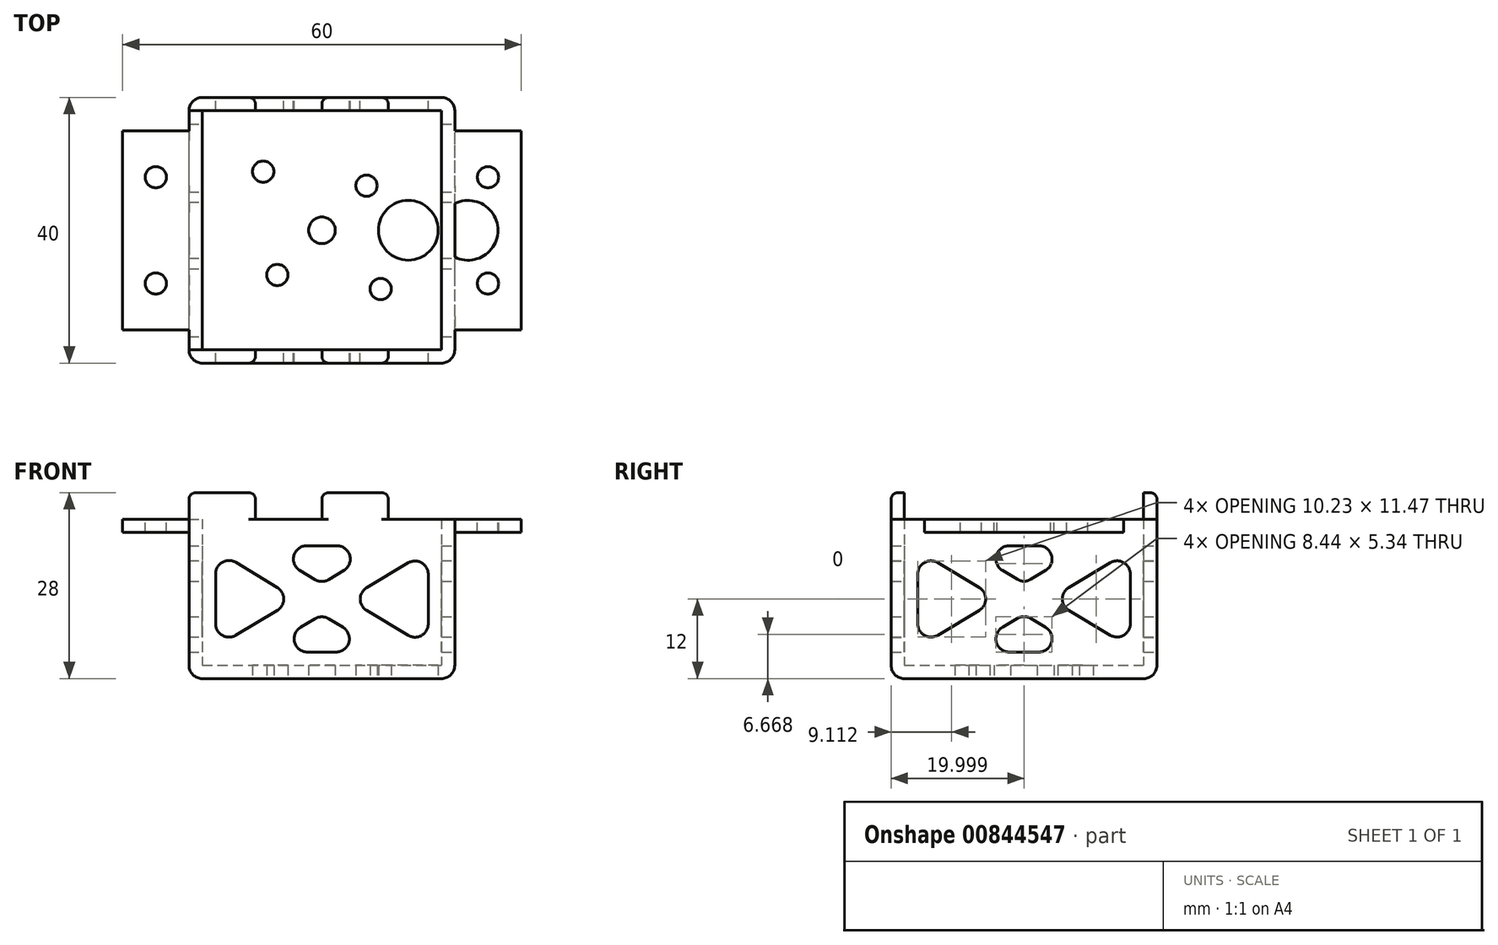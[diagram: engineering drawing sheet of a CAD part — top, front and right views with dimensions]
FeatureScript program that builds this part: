
annotation { "Feature Type Name" : "Feature", "Feature Type Description" : "" }
export const myFeature = defineFeature(function(context is Context, id is Id, definition is map)
    precondition{}
    {
        {
            var Q0;
            Q0=qCreatedBy(makeId("Top.planeOp"),FACE);
            var sketch = newSketch(context, id + "F0", { "sketchPlane" : qUnion([Q0])});
            skLineSegment(sketch, "E0.bottom", {"start": v(-66.54, 9.74) * mm, "end": v(-26.54, 9.74) * mm});
            skLineSegment(sketch, "E0.top", {"start": v(-66.54, 49.74) * mm, "end": v(-26.54, 49.74) * mm});
            skLineSegment(sketch, "E0.left", {"start": v(-66.54, 9.74) * mm, "end": v(-66.54, 49.74) * mm});
            skLineSegment(sketch, "E0.right", {"start": v(-26.54, 9.74) * mm, "end": v(-26.54, 49.74) * mm});
            skPoint(sketch, "E1", {"position": v(-46.54, 29.74) * mm});
            skPoint(sketch, "E1.positionSnap0", {"position": v(-46.54, 49.74) * mm});
            skPoint(sketch, "E1.positionSnap1", {"position": v(-26.54, 29.74) * mm});
            skPoint(sketch, "E2", {"position": v(-55.38, 38.58) * mm});
            skPoint(sketch, "E3", {"position": v(-37.7, 20.9) * mm});
            skPoint(sketch, "E4", {"position": v(-53.26, 23.02) * mm});
            skPoint(sketch, "E5", {"position": v(-39.82, 36.46) * mm});
            skPoint(sketch, "E6", {"position": v(-33.54, 29.74) * mm});
            skSolve(sketch);
        }
        {
            var Q0;
            Q0=makeQuery(id+"F0.imprint","IMPRINT",FACE,{"disambiguationData":[TD([[makeQuery(id+"F0.imprint","IMPRINT",EDGE,{"derivedFrom":sQuery(id+"F0.wireOp",EDGE,"E0.bottom")}),1.0]])]});
            extrude(context, id + "F1", {"entities" : qUnion([Q0]), "depth" : 2 * mm, "offsetDistance" : 25 * mm});
        }
        {
            var Q0;
            Q0=makeQuery(id+"F1.opExtrude","CAP_FACE",FACE,{"disambiguationData":[OSD([sQuery(id+"F0.wireOp",EDGE,"E0.bottom"),sQuery(id+"F0.wireOp",EDGE,"E0.top"),sQuery(id+"F0.wireOp",EDGE,"E0.left"),sQuery(id+"F0.wireOp",EDGE,"E0.right")])],"isStart":false});
            var sketch = newSketch(context, id + "F2", { "sketchPlane" : qUnion([Q0])});
            skLineSegment(sketch, "E7.bottom", {"start": v(-66.54, 9.74) * mm, "end": v(-26.54, 9.74) * mm});
            skLineSegment(sketch, "E7.top", {"start": v(-66.54, 49.74) * mm, "end": v(-26.54, 49.74) * mm});
            skLineSegment(sketch, "E7.left", {"start": v(-66.54, 9.74) * mm, "end": v(-66.54, 49.74) * mm});
            skLineSegment(sketch, "E7.right", {"start": v(-26.54, 9.74) * mm, "end": v(-26.54, 49.74) * mm});
            skLineSegment(sketch, "E8.0", {"start": v(-28.54, 11.74) * mm, "end": v(-28.54, 47.74) * mm});
            skLineSegment(sketch, "E8.1", {"start": v(-64.54, 11.74) * mm, "end": v(-28.54, 11.74) * mm});
            skLineSegment(sketch, "E8.2", {"start": v(-64.54, 11.74) * mm, "end": v(-64.54, 47.74) * mm});
            skLineSegment(sketch, "E8.3", {"start": v(-64.54, 47.74) * mm, "end": v(-28.54, 47.74) * mm});
            skSolve(sketch);
        }
        {
            var Q0;
            Q0=makeQuery(id+"F2.imprint","IMPRINT",FACE,{"disambiguationData":[TD([[makeQuery(id+"F2.imprint","IMPRINT",EDGE,{"derivedFrom":sQuery(id+"F2.wireOp",EDGE,"E7.bottom")}),1.0]])]});
            extrude(context, id + "F3", {"entities" : qUnion([Q0]), "operationType" : NewBodyOperationType.ADD, "depth" : 22 * mm, "offsetDistance" : 25 * mm});
        }
        {
            var Q0;
            Q0=makeQuery(id+"F3.boolean.opBoolean","MERGE",FACE,{"derivedFrom":[makeQuery(id+"F1.opExtrude","SWEPT_FACE",FACE,{"disambiguationData":[OSD([sQuery(id+"F0.wireOp",EDGE,"E0.bottom")])]}),makeQuery(id+"F3.opExtrude","SWEPT_FACE",FACE,{"disambiguationData":[OSD([sQuery(id+"F2.wireOp",EDGE,"E7.bottom")])]})]});
            var sketch = newSketch(context, id + "F4", { "sketchPlane" : qUnion([Q0])});
            skLineSegment(sketch, "E9", {"start": v(-66.54, 24) * mm, "end": v(-66.54, 28) * mm});
            skLineSegment(sketch, "E10", {"start": v(-66.54, 28) * mm, "end": v(-56.54, 28) * mm});
            skLineSegment(sketch, "E11", {"start": v(-56.54, 28) * mm, "end": v(-56.54, 24) * mm});
            skLineSegment(sketch, "E12.MirrorCS", {"start": v(-36.54, 28) * mm, "end": v(-46.54, 28) * mm});
            skLineSegment(sketch, "E13.MirrorCS", {"start": v(-46.54, 28) * mm, "end": v(-46.54, 24) * mm});
            skLineSegment(sketch, "E14.MirrorCS", {"start": v(-36.54, 24) * mm, "end": v(-36.54, 28) * mm});
            skSolve(sketch);
        }
        {
            var Q0;
            Q0=makeQuery(id+"F4.imprint","IMPRINT",FACE,{"disambiguationData":[TD([[makeQuery(id+"F4.imprint","IMPRINT",EDGE,{"derivedFrom":sQuery(id+"F4.wireOp",EDGE,"E12.MirrorCS")}),1.0]])]});
            var Q1;
            {var subQ0=sQuery(id+"F4.wireOp",EDGE,"E9");Q1=makeQuery(id+"F4.imprint","IMPRINT",FACE,{"disambiguationData":[TD([[makeQuery(id+"F4.imprint","IMPRINT",EDGE,{"derivedFrom":subQ0}),-1.0]])]});}
            var Q2;
            Q2=makeQuery(id+"F3.opExtrude","SWEPT_FACE",FACE,{"disambiguationData":[OSD([sQuery(id+"F2.wireOp",EDGE,"E8.1")])]});
            extrude(context, id + "F5", {"entities" : qUnion([Q0, Q1]), "operationType" : NewBodyOperationType.ADD, "endBound" : BoundingType.UP_TO_SURFACE, "oppositeDirection" : true, "depth" : 8.5 * mm, "endBoundEntityFace" : qUnion([Q2]), "offsetDistance" : 25 * mm});
        }
        {
            var Q0;
            Q0=makeQuery(id+"F3.boolean.opBoolean","MERGE",FACE,{"derivedFrom":[makeQuery(id+"F1.opExtrude","SWEPT_FACE",FACE,{"disambiguationData":[OSD([sQuery(id+"F0.wireOp",EDGE,"E0.top")])]}),makeQuery(id+"F3.opExtrude","SWEPT_FACE",FACE,{"disambiguationData":[OSD([sQuery(id+"F2.wireOp",EDGE,"E7.top")])]})]});
            var sketch = newSketch(context, id + "F6", { "sketchPlane" : qUnion([Q0])});
            skLineSegment(sketch, "E15", {"start": v(36.54, 24) * mm, "end": v(36.54, 28) * mm});
            skLineSegment(sketch, "E16", {"start": v(36.54, 28) * mm, "end": v(46.54, 28) * mm});
            skLineSegment(sketch, "E17", {"start": v(46.54, 28) * mm, "end": v(46.54, 24) * mm});
            skLineSegment(sketch, "E18", {"start": v(56.54, 24) * mm, "end": v(56.54, 28) * mm});
            skLineSegment(sketch, "E19", {"start": v(56.54, 28) * mm, "end": v(66.54, 28) * mm});
            skLineSegment(sketch, "E20", {"start": v(66.54, 28) * mm, "end": v(66.54, 24) * mm});
            skSolve(sketch);
        }
        {
            var Q0;
            {var subQ0=sQuery(id+"F6.wireOp",EDGE,"E15");Q0=makeQuery(id+"F6.imprint","IMPRINT",FACE,{"disambiguationData":[TD([[makeQuery(id+"F6.imprint","IMPRINT",EDGE,{"derivedFrom":subQ0}),-1.0]])]});}
            var Q1;
            {var subQ0=sQuery(id+"F6.wireOp",EDGE,"E18");Q1=makeQuery(id+"F6.imprint","IMPRINT",FACE,{"disambiguationData":[TD([[makeQuery(id+"F6.imprint","IMPRINT",EDGE,{"derivedFrom":subQ0}),-1.0]])]});}
            var Q2;
            Q2=makeQuery(id+"F3.opExtrude","SWEPT_FACE",FACE,{"disambiguationData":[OSD([sQuery(id+"F2.wireOp",EDGE,"E8.3")])]});
            extrude(context, id + "F7", {"entities" : qUnion([Q0, Q1]), "operationType" : NewBodyOperationType.ADD, "endBound" : BoundingType.UP_TO_SURFACE, "oppositeDirection" : true, "depth" : 25 * mm, "endBoundEntityFace" : qUnion([Q2]), "offsetDistance" : 25 * mm});
        }
        {
            var Q0;
            {var subQ0=sQuery(id+"F2.wireOp",EDGE,"E8.3");var subQ2=sQuery(id+"F2.wireOp",EDGE,"E8.1");var subQ5=sQuery(id+"F2.wireOp",EDGE,"E7.bottom");var subQ7=sQuery(id+"F2.wireOp",EDGE,"E8.0");var subQ9=sQuery(id+"F2.wireOp",EDGE,"E7.right");var subQ11=sQuery(id+"F2.wireOp",EDGE,"E7.top");var subQ15=makeQuery(id+"F1.opExtrude","SWEPT_FACE",FACE,{"disambiguationData":[OSD([sQuery(id+"F0.wireOp",EDGE,"E0.right")])]});var subQ17=makeQuery(id+"F1.opExtrude","SWEPT_FACE",FACE,{"disambiguationData":[OSD([sQuery(id+"F0.wireOp",EDGE,"E0.top")])]});var subQ23=sQuery(id+"F2.wireOp",EDGE,"E7.left");var subQ24=sQuery(id+"F2.wireOp",EDGE,"E8.2");Q0=makeQuery(id+"F7.boolean.opBoolean","SPLIT",FACE,{"disambiguationData":[TD([subQ15])],"derivedFrom":makeQuery(id+"F5.boolean.opBoolean","SPLIT",FACE,{"disambiguationData":[TD([subQ17])],"derivedFrom":makeQuery(id+"F3.opExtrude","CAP_FACE",FACE,{"disambiguationData":[OSD([subQ5,subQ11,subQ23,subQ9,subQ7,subQ2,subQ24,subQ0])],"isStart":false})})});}
            var sketch = newSketch(context, id + "F8", { "sketchPlane" : qUnion([Q0])});
            skLineSegment(sketch, "E21", {"start": v(-26.54, 44.74) * mm, "end": v(-16.54, 44.74) * mm});
            skLineSegment(sketch, "E22", {"start": v(-16.54, 44.74) * mm, "end": v(-16.54, 14.74) * mm});
            skLineSegment(sketch, "E23", {"start": v(-16.54, 14.74) * mm, "end": v(-26.54, 14.74) * mm});
            skPoint(sketch, "E24", {"position": v(-21.54, 21.74) * mm});
            skPoint(sketch, "E24.positionSnap0", {"position": v(-21.54, 14.74) * mm});
            skPoint(sketch, "E25", {"position": v(-21.54, 37.74) * mm});
            skPoint(sketch, "E26", {"position": v(-24.54, 29.74) * mm});
            skPoint(sketch, "E26.positionSnap0", {"position": v(-26.54, 29.74) * mm});
            skCircle(sketch, "E27", {"center": v(-24.54, 29.74) * mm, "radius": 4.5 * mm});
            skSolve(sketch);
        }
        {
            var Q0;
            {var subQ0=sQuery(id+"F8.wireOp",EDGE,"E21");Q0=makeQuery(id+"F8.imprint","IMPRINT",FACE,{"disambiguationData":[TD([[makeQuery(id+"F8.imprint","IMPRINT",EDGE,{"derivedFrom":subQ0}),-1.0]])]});}
            extrude(context, id + "F9", {"entities" : qUnion([Q0]), "operationType" : NewBodyOperationType.ADD, "oppositeDirection" : true, "depth" : 2 * mm, "offsetDistance" : 25 * mm});
        }
        {
            var Q0;
            {var subQ2=sQuery(id+"F2.wireOp",EDGE,"E8.3");var subQ4=sQuery(id+"F2.wireOp",EDGE,"E8.2");var subQ7=sQuery(id+"F2.wireOp",EDGE,"E7.top");var subQ8=sQuery(id+"F2.wireOp",EDGE,"E8.1");var subQ10=sQuery(id+"F2.wireOp",EDGE,"E7.left");var subQ13=makeQuery(id+"F1.opExtrude","SWEPT_FACE",FACE,{"disambiguationData":[OSD([sQuery(id+"F0.wireOp",EDGE,"E0.top")])]});var subQ14=sQuery(id+"F2.wireOp",EDGE,"E7.bottom");var subQ16=makeQuery(id+"F1.opExtrude","SWEPT_FACE",FACE,{"disambiguationData":[OSD([sQuery(id+"F0.wireOp",EDGE,"E0.left")])]});var subQ23=sQuery(id+"F2.wireOp",EDGE,"E8.0");var subQ24=sQuery(id+"F2.wireOp",EDGE,"E7.right");Q0=makeQuery(id+"F7.boolean.opBoolean","SPLIT",FACE,{"disambiguationData":[TD([subQ16])],"derivedFrom":makeQuery(id+"F5.boolean.opBoolean","SPLIT",FACE,{"disambiguationData":[TD([subQ13])],"derivedFrom":makeQuery(id+"F3.opExtrude","CAP_FACE",FACE,{"disambiguationData":[OSD([subQ14,subQ7,subQ10,subQ24,subQ23,subQ8,subQ4,subQ2])],"isStart":false})})});}
            var sketch = newSketch(context, id + "F10", { "sketchPlane" : qUnion([Q0])});
            skLineSegment(sketch, "E28", {"start": v(-76.54, 44.74) * mm, "end": v(-76.54, 14.74) * mm});
            skLineSegment(sketch, "E29", {"start": v(-76.54, 14.74) * mm, "end": v(-66.54, 14.74) * mm});
            skLineSegment(sketch, "E30", {"start": v(-66.54, 44.74) * mm, "end": v(-76.54, 44.74) * mm});
            skPoint(sketch, "E31", {"position": v(-71.54, 21.74) * mm});
            skPoint(sketch, "E31.positionSnap0", {"position": v(-71.54, 14.74) * mm});
            skPoint(sketch, "E32", {"position": v(-71.54, 37.74) * mm});
            skSolve(sketch);
        }
        {
            var Q0;
            Q0=makeQuery(id+"F10.imprint","IMPRINT",FACE,{"disambiguationData":[TD([[makeQuery(id+"F10.imprint","IMPRINT",EDGE,{"derivedFrom":sQuery(id+"F10.wireOp",EDGE,"E28")}),1.0]])]});
            extrude(context, id + "F11", {"entities" : qUnion([Q0]), "operationType" : NewBodyOperationType.ADD, "oppositeDirection" : true, "depth" : 2 * mm, "offsetDistance" : 25 * mm});
        }
        {
            var Q0;
            Q0=sQuery(id+"F8.wireOp",VERTEX,"E24");
            var Q1;
            Q1=sQuery(id+"F8.wireOp",VERTEX,"E25");
            var Q2;
            Q2=sQuery(id+"F10.wireOp",VERTEX,"E31");
            var Q3;
            Q3=sQuery(id+"F10.wireOp",VERTEX,"E32");
            var Q4;
            Q4=makeQuery(id+"F1.opExtrude","SWEPT_BODY",BODY,{"disambiguationData":[OSD([sQuery(id+"F0.wireOp",EDGE,"E0.bottom"),sQuery(id+"F0.wireOp",EDGE,"E0.top"),sQuery(id+"F0.wireOp",EDGE,"E0.left"),sQuery(id+"F0.wireOp",EDGE,"E0.right")])]});
            hole(context, id + "F12", {"style" : HoleStyle.SIMPLE, "endStyle" : HoleEndStyle.THROUGH, "holeDiameter" : 3.2 * mm, "majorDiameter" : 5 * mm, "isTappedThrough" : true, "tappedDepth" : 12 * mm, "tapClearance" : 3, "startFromSketch" : true, "locations" : qUnion([Q0, Q1, Q2, Q3]), "scope" : qUnion([Q4])});
        }
        {
            var Q0;
            Q0=sQuery(id+"F0.wireOp",VERTEX,"E5");
            var Q1;
            Q1=sQuery(id+"F0.wireOp",VERTEX,"E2");
            var Q2;
            Q2=sQuery(id+"F0.wireOp",VERTEX,"E4");
            var Q3;
            Q3=sQuery(id+"F0.wireOp",VERTEX,"E3");
            var Q4;
            Q4=makeQuery(id+"F1.opExtrude","SWEPT_BODY",BODY,{"disambiguationData":[OSD([sQuery(id+"F0.wireOp",EDGE,"E0.bottom"),sQuery(id+"F0.wireOp",EDGE,"E0.top"),sQuery(id+"F0.wireOp",EDGE,"E0.left"),sQuery(id+"F0.wireOp",EDGE,"E0.right")])]});
            hole(context, id + "F13", {"style" : HoleStyle.SIMPLE, "endStyle" : HoleEndStyle.THROUGH, "oppositeDirection" : true, "holeDiameter" : 3.2 * mm, "majorDiameter" : 5 * mm, "isTappedThrough" : true, "tappedDepth" : 12 * mm, "tapClearance" : 3, "startFromSketch" : true, "locations" : qUnion([Q0, Q1, Q2, Q3]), "scope" : qUnion([Q4])});
        }
        {
            var Q0;
            Q0=sQuery(id+"F0.wireOp",VERTEX,"E6");
            var Q1;
            Q1=makeQuery(id+"F1.opExtrude","SWEPT_BODY",BODY,{"disambiguationData":[OSD([sQuery(id+"F0.wireOp",EDGE,"E0.bottom"),sQuery(id+"F0.wireOp",EDGE,"E0.top"),sQuery(id+"F0.wireOp",EDGE,"E0.left"),sQuery(id+"F0.wireOp",EDGE,"E0.right")])]});
            hole(context, id + "F14", {"style" : HoleStyle.SIMPLE, "endStyle" : HoleEndStyle.THROUGH, "oppositeDirection" : true, "holeDiameter" : 9 * mm, "majorDiameter" : 5 * mm, "isTappedThrough" : true, "tappedDepth" : 12 * mm, "tapClearance" : 3, "startFromSketch" : true, "locations" : qUnion([Q0]), "scope" : qUnion([Q1])});
        }
        {
            var Q0;
            Q0=sQuery(id+"F0.wireOp",VERTEX,"E1");
            var Q1;
            Q1=makeQuery(id+"F1.opExtrude","SWEPT_BODY",BODY,{"disambiguationData":[OSD([sQuery(id+"F0.wireOp",EDGE,"E0.bottom"),sQuery(id+"F0.wireOp",EDGE,"E0.top"),sQuery(id+"F0.wireOp",EDGE,"E0.left"),sQuery(id+"F0.wireOp",EDGE,"E0.right")])]});
            hole(context, id + "F15", {"style" : HoleStyle.SIMPLE, "endStyle" : HoleEndStyle.THROUGH, "oppositeDirection" : true, "holeDiameter" : 4 * mm, "majorDiameter" : 5 * mm, "isTappedThrough" : true, "tappedDepth" : 12 * mm, "tapClearance" : 3, "startFromSketch" : true, "locations" : qUnion([Q0]), "scope" : qUnion([Q1])});
        }
        {
            var Q0;
            Q0=makeQuery(id+"F7.opExtrude","CAP_EDGE",EDGE,{"disambiguationData":[OSD([sQuery(id+"F6.wireOp",EDGE,"E15")])],"isStart":true});
            var Q1;
            Q1=makeQuery(id+"F7.opExtrude","TWEAK_EDGE",EDGE,{"derivedFrom":[makeQuery(id+"F3.opExtrude","SWEPT_FACE",FACE,{"disambiguationData":[OSD([sQuery(id+"F2.wireOp",EDGE,"E8.3")])]}),makeQuery(id+"F6.imprint","IMPRINT",EDGE,{"derivedFrom":sQuery(id+"F6.wireOp",EDGE,"E15")})]});
            var Q2;
            Q2=makeQuery(id+"F7.opExtrude","CAP_EDGE",EDGE,{"disambiguationData":[OSD([sQuery(id+"F6.wireOp",EDGE,"E17")])],"isStart":true});
            var Q3;
            Q3=makeQuery(id+"F7.opExtrude","TWEAK_EDGE",EDGE,{"derivedFrom":[makeQuery(id+"F3.opExtrude","SWEPT_FACE",FACE,{"disambiguationData":[OSD([sQuery(id+"F2.wireOp",EDGE,"E8.3")])]}),makeQuery(id+"F6.imprint","IMPRINT",EDGE,{"derivedFrom":sQuery(id+"F6.wireOp",EDGE,"E17")})]});
            var Q4;
            Q4=makeQuery(id+"F7.opExtrude","TWEAK_EDGE",EDGE,{"derivedFrom":[makeQuery(id+"F3.opExtrude","SWEPT_FACE",FACE,{"disambiguationData":[OSD([sQuery(id+"F2.wireOp",EDGE,"E8.3")])]}),makeQuery(id+"F6.imprint","IMPRINT",EDGE,{"derivedFrom":sQuery(id+"F6.wireOp",EDGE,"E18")})]});
            var Q5;
            Q5=makeQuery(id+"F7.opExtrude","CAP_EDGE",EDGE,{"disambiguationData":[OSD([sQuery(id+"F6.wireOp",EDGE,"E18")])],"isStart":true});
            var Q6;
            Q6=makeQuery(id+"F5.opExtrude","CAP_EDGE",EDGE,{"disambiguationData":[OSD([sQuery(id+"F4.wireOp",EDGE,"E11")])],"isStart":true});
            var Q7;
            Q7=makeQuery(id+"F5.opExtrude","CAP_EDGE",EDGE,{"disambiguationData":[OSD([sQuery(id+"F4.wireOp",EDGE,"E13.MirrorCS")])],"isStart":true});
            var Q8;
            Q8=makeQuery(id+"F5.opExtrude","CAP_EDGE",EDGE,{"disambiguationData":[OSD([sQuery(id+"F4.wireOp",EDGE,"E14.MirrorCS")])],"isStart":true});
            var Q9;
            {var subQ0=sQuery(id+"F4.wireOp",EDGE,"E14.MirrorCS");Q9=makeQuery(id+"F5.opExtrude","TWEAK_EDGE",EDGE,{"derivedFrom":[makeQuery(id+"F3.opExtrude","SWEPT_FACE",FACE,{"disambiguationData":[OSD([sQuery(id+"F2.wireOp",EDGE,"E8.1")])]}),makeQuery(id+"F4.imprint","IMPRINT",EDGE,{"disambiguationData":[TD([[makeQuery(id+"F4.imprint","INTERSECT",VERTEX,{"derivedFrom":[sQuery(id+"F4.wireOp",EDGE,"E12.MirrorCS"),subQ0]}),1.0]])],"derivedFrom":subQ0})]});}
            var Q10;
            Q10=makeQuery(id+"F5.opExtrude","TWEAK_EDGE",EDGE,{"derivedFrom":[makeQuery(id+"F3.opExtrude","SWEPT_FACE",FACE,{"disambiguationData":[OSD([sQuery(id+"F2.wireOp",EDGE,"E8.1")])]}),makeQuery(id+"F4.imprint","IMPRINT",EDGE,{"derivedFrom":sQuery(id+"F4.wireOp",EDGE,"E11")})]});
            var Q11;
            Q11=makeQuery(id+"F5.opExtrude","TWEAK_EDGE",EDGE,{"derivedFrom":[makeQuery(id+"F3.opExtrude","SWEPT_FACE",FACE,{"disambiguationData":[OSD([sQuery(id+"F2.wireOp",EDGE,"E8.1")])]}),makeQuery(id+"F4.imprint","IMPRINT",EDGE,{"derivedFrom":sQuery(id+"F4.wireOp",EDGE,"E13.MirrorCS")})]});
            fillet(context, id + "F16", {"entities" : qUnion([Q0, Q1, Q2, Q3, Q4, Q5, Q6, Q7, Q8, Q9, Q10, Q11]), "radius" : 1 * mm, "tangentPropagation" : true, "allowEdgeOverflow" : false});
        }
        {
            var Q0;
            Q0=makeQuery(id+"F3.boolean.opBoolean","MERGE",FACE,{"derivedFrom":[makeQuery(id+"F1.opExtrude","SWEPT_FACE",FACE,{"disambiguationData":[OSD([sQuery(id+"F0.wireOp",EDGE,"E0.right")])]}),makeQuery(id+"F3.opExtrude","SWEPT_FACE",FACE,{"disambiguationData":[OSD([sQuery(id+"F2.wireOp",EDGE,"E7.right")])]})]});
            var sketch = newSketch(context, id + "F17", { "sketchPlane" : qUnion([Q0])});
            skLineSegment(sketch, "E33.0", {"start": v(13.74, 24) * mm, "end": v(13.74, 23.93) * mm});
            skLineSegment(sketch, "E34.0", {"start": v(27.51, 20) * mm, "end": v(31.96, 20) * mm});
            skLineSegment(sketch, "E35.0", {"start": v(42.71, 17.45) * mm, "end": v(36.48, 13.71) * mm});
            skLineSegment(sketch, "E36.0", {"start": v(33, 16.29) * mm, "end": v(30.77, 14.95) * mm});
            skLineSegment(sketch, "E37.trimOffspring", {"start": v(29.74, 12) * mm, "end": v(29.74, 12) * mm});
            skLineSegment(sketch, "E38.trimOffspring", {"start": v(36.48, 10.29) * mm, "end": v(42.71, 6.55) * mm});
            skLineSegment(sketch, "E39.trimOffspring", {"start": v(31.68, 13.17) * mm, "end": v(31.69, 13.16) * mm});
            skLineSegment(sketch, "E40.trimOffspring", {"start": v(23, 10.29) * mm, "end": v(16.77, 6.55) * mm});
            skLineSegment(sketch, "E41.trimOffspring", {"start": v(30.77, 9.05) * mm, "end": v(33, 7.71) * mm});
            skLineSegment(sketch, "E42.trimOffspring", {"start": v(28.71, 9.05) * mm, "end": v(26.48, 7.71) * mm});
            skLineSegment(sketch, "E43.trimOffspring", {"start": v(45.74, 15.74) * mm, "end": v(45.74, 8.26) * mm});
            skLineSegment(sketch, "E44.trimOffspring", {"start": v(26.48, 16.29) * mm, "end": v(28.71, 14.95) * mm});
            skLineSegment(sketch, "E45.trimOffspring", {"start": v(45.74, 0.07) * mm, "end": v(45.74, 0) * mm});
            skLineSegment(sketch, "E46.trimOffspring", {"start": v(27.51, 4) * mm, "end": v(31.96, 4) * mm});
            skLineSegment(sketch, "E47.trimOffspring", {"start": v(16.4, 4) * mm, "end": v(16.41, 4) * mm});
            skLineSegment(sketch, "E48.trimOffspring", {"start": v(13.74, 15.74) * mm, "end": v(13.74, 8.26) * mm});
            skLineSegment(sketch, "E49", {"start": v(16.77, 17.45) * mm, "end": v(23, 13.71) * mm});
            skPoint(sketch, "E50.visualSharp", {"position": v(25.85, 12) * mm});
            skArc(sketch, "E50.filletArc", {"start": v(23, 10.29) * mm, "mid": v(23.96, 12) * mm, "end": v(23, 13.71) * mm});
            skPoint(sketch, "E51.visualSharp", {"position": v(13.74, 19.27) * mm});
            skArc(sketch, "E51.filletArc", {"start": v(16.77, 17.45) * mm, "mid": v(14.75, 17.48) * mm, "end": v(13.74, 15.74) * mm});
            skPoint(sketch, "E52.visualSharp", {"position": v(13.74, 4.73) * mm});
            skArc(sketch, "E52.filletArc", {"start": v(13.74, 8.26) * mm, "mid": v(14.75, 6.52) * mm, "end": v(16.77, 6.55) * mm});
            skPoint(sketch, "E53.visualSharp", {"position": v(29.74, 14.33) * mm});
            skArc(sketch, "E53.filletArc", {"start": v(28.71, 14.95) * mm, "mid": v(29.74, 14.66) * mm, "end": v(30.77, 14.95) * mm});
            skPoint(sketch, "E54.visualSharp", {"position": v(39.19, 20) * mm});
            skArc(sketch, "E54.filletArc", {"start": v(33, 16.29) * mm, "mid": v(33.9, 18.53) * mm, "end": v(31.96, 20) * mm});
            skPoint(sketch, "E55.visualSharp", {"position": v(20.3, 20) * mm});
            skArc(sketch, "E55.filletArc", {"start": v(27.51, 20) * mm, "mid": v(25.59, 18.53) * mm, "end": v(26.48, 16.29) * mm});
            skPoint(sketch, "E56.visualSharp", {"position": v(33.63, 12) * mm});
            skArc(sketch, "E56.filletArc", {"start": v(36.48, 13.71) * mm, "mid": v(35.51, 12) * mm, "end": v(36.48, 10.29) * mm});
            skPoint(sketch, "E57.visualSharp", {"position": v(45.74, 4.73) * mm});
            skArc(sketch, "E57.filletArc", {"start": v(42.71, 6.55) * mm, "mid": v(44.72, 6.52) * mm, "end": v(45.74, 8.26) * mm});
            skPoint(sketch, "E58.visualSharp", {"position": v(45.74, 19.27) * mm});
            skArc(sketch, "E58.filletArc", {"start": v(45.74, 15.74) * mm, "mid": v(44.72, 17.48) * mm, "end": v(42.71, 17.45) * mm});
            skPoint(sketch, "E59.visualSharp", {"position": v(29.74, 9.67) * mm});
            skArc(sketch, "E59.filletArc", {"start": v(30.77, 9.05) * mm, "mid": v(29.74, 9.34) * mm, "end": v(28.71, 9.05) * mm});
            skPoint(sketch, "E60.visualSharp", {"position": v(20.3, 4) * mm});
            skArc(sketch, "E60.filletArc", {"start": v(26.48, 7.71) * mm, "mid": v(25.59, 5.47) * mm, "end": v(27.51, 4) * mm});
            skPoint(sketch, "E61.visualSharp", {"position": v(39.19, 4) * mm});
            skArc(sketch, "E61.filletArc", {"start": v(31.96, 4) * mm, "mid": v(33.9, 5.47) * mm, "end": v(33, 7.71) * mm});
            skSolve(sketch);
        }
        {
            var Q0;
            Q0=makeQuery(id+"F17.imprint","IMPRINT",FACE,{"disambiguationData":[TD([[makeQuery(id+"F17.imprint","IMPRINT",EDGE,{"derivedFrom":sQuery(id+"F17.wireOp",EDGE,"E40.trimOffspring")}),-1.0]])]});
            var Q1;
            Q1=makeQuery(id+"F17.imprint","IMPRINT",FACE,{"disambiguationData":[TD([[makeQuery(id+"F17.imprint","IMPRINT",EDGE,{"derivedFrom":sQuery(id+"F17.wireOp",EDGE,"E34.0")}),-1.0]])]});
            var Q2;
            Q2=makeQuery(id+"F17.imprint","IMPRINT",FACE,{"disambiguationData":[TD([[makeQuery(id+"F17.imprint","IMPRINT",EDGE,{"derivedFrom":sQuery(id+"F17.wireOp",EDGE,"E35.0")}),1.0]])]});
            var Q3;
            Q3=makeQuery(id+"F17.imprint","IMPRINT",FACE,{"disambiguationData":[TD([[makeQuery(id+"F17.imprint","IMPRINT",EDGE,{"derivedFrom":sQuery(id+"F17.wireOp",EDGE,"E41.trimOffspring")}),-1.0]])]});
            var Q4;
            Q4=makeQuery(id+"F7.boolean.opBoolean","MERGE",FACE,{"derivedFrom":[makeQuery(id+"F5.boolean.opBoolean","MERGE",FACE,{"derivedFrom":[makeQuery(id+"F3.boolean.opBoolean","MERGE",FACE,{"derivedFrom":[makeQuery(id+"F1.opExtrude","SWEPT_FACE",FACE,{"disambiguationData":[OSD([sQuery(id+"F0.wireOp",EDGE,"E0.left")])]}),makeQuery(id+"F3.opExtrude","SWEPT_FACE",FACE,{"disambiguationData":[OSD([sQuery(id+"F2.wireOp",EDGE,"E7.left")])]})]}),makeQuery(id+"F5.opExtrude","SWEPT_FACE",FACE,{"disambiguationData":[OSD([sQuery(id+"F4.wireOp",EDGE,"E9")])]})]}),makeQuery(id+"F7.opExtrude","SWEPT_FACE",FACE,{"disambiguationData":[OSD([sQuery(id+"F6.wireOp",EDGE,"E20")])]})]});
            extrude(context, id + "F18", {"entities" : qUnion([Q0, Q1, Q2, Q3]), "operationType" : NewBodyOperationType.REMOVE, "endBound" : BoundingType.UP_TO_SURFACE, "oppositeDirection" : true, "depth" : 25 * mm, "endBoundEntityFace" : qUnion([Q4]), "offsetDistance" : 25 * mm});
        }
        {
            var Q0;
            {var subQ0=sQuery(id+"F2.wireOp",EDGE,"E7.top");Q0=makeQuery(id+"F7.boolean.opBoolean","MERGE",FACE,{"derivedFrom":[makeQuery(id+"F3.boolean.opBoolean","MERGE",FACE,{"derivedFrom":[makeQuery(id+"F1.opExtrude","SWEPT_FACE",FACE,{"disambiguationData":[OSD([sQuery(id+"F0.wireOp",EDGE,"E0.top")])]}),makeQuery(id+"F3.opExtrude","SWEPT_FACE",FACE,{"disambiguationData":[OSD([subQ0])]})]}),makeQuery(id+"F7.opExtrude","CAP_FACE",FACE,{"disambiguationData":[OSD([subQ0,sQuery(id+"F6.wireOp",EDGE,"E15"),sQuery(id+"F6.wireOp",EDGE,"E16"),sQuery(id+"F6.wireOp",EDGE,"E17")])],"isStart":true}),makeQuery(id+"F7.opExtrude","CAP_FACE",FACE,{"disambiguationData":[OSD([subQ0,sQuery(id+"F6.wireOp",EDGE,"E18"),sQuery(id+"F6.wireOp",EDGE,"E19"),sQuery(id+"F6.wireOp",EDGE,"E20")])],"isStart":true})]});}
            var sketch = newSketch(context, id + "F19", { "sketchPlane" : qUnion([Q0])});
            skLineSegment(sketch, "E62.0", {"start": v(43.37, 7.71) * mm, "end": v(45.52, 9.01) * mm});
            skLineSegment(sketch, "E63.0", {"start": v(33.57, 6.51) * mm, "end": v(39.8, 10.26) * mm});
            skLineSegment(sketch, "E64.0", {"start": v(33.57, 17.43) * mm, "end": v(39.8, 13.69) * mm});
            skPoint(sketch, "E65.orphan", {"position": v(66.54, 24) * mm});
            skLineSegment(sketch, "E66.trimOffspring", {"start": v(53.25, 13.7) * mm, "end": v(59.5, 17.5) * mm});
            skLineSegment(sketch, "E67.trimOffspring", {"start": v(53.26, 10.28) * mm, "end": v(59.51, 6.53) * mm});
            skLineSegment(sketch, "E68.trimOffspring", {"start": v(47.58, 9.02) * mm, "end": v(49.75, 7.71) * mm});
            skLineSegment(sketch, "E69.trimOffspring", {"start": v(47.58, 14.92) * mm, "end": v(49.85, 16.29) * mm});
            skLineSegment(sketch, "E70.0", {"start": v(62.54, 15.78) * mm, "end": v(62.54, 8.24) * mm});
            skLineSegment(sketch, "E71.0", {"start": v(30.54, 24) * mm, "end": v(30.54, 23.9) * mm});
            skLineSegment(sketch, "E72.0", {"start": v(48.83, 20) * mm, "end": v(44.27, 20) * mm});
            skLineSegment(sketch, "E73.trimOffspring", {"start": v(62.54, 0.04) * mm, "end": v(62.54, 0) * mm});
            skLineSegment(sketch, "E74.trimOffspring", {"start": v(48.73, 4) * mm, "end": v(44.4, 4) * mm});
            skLineSegment(sketch, "E75.trimOffspring", {"start": v(43.25, 16.29) * mm, "end": v(45.52, 14.92) * mm});
            skLineSegment(sketch, "E76.trimOffspring", {"start": v(30.54, 15.71) * mm, "end": v(30.54, 8.23) * mm});
            skPoint(sketch, "E77.0.start.orphan", {"position": v(27.56, 25.7) * mm});
            skPoint(sketch, "E78.visualSharp", {"position": v(46.55, 14.3) * mm});
            skArc(sketch, "E78.filletArc", {"start": v(45.52, 14.92) * mm, "mid": v(46.55, 14.63) * mm, "end": v(47.58, 14.92) * mm});
            skPoint(sketch, "E79.visualSharp", {"position": v(56.05, 20) * mm});
            skArc(sketch, "E79.filletArc", {"start": v(49.85, 16.29) * mm, "mid": v(50.75, 18.53) * mm, "end": v(48.83, 20) * mm});
            skPoint(sketch, "E80.visualSharp", {"position": v(37.05, 20) * mm});
            skArc(sketch, "E80.filletArc", {"start": v(44.27, 20) * mm, "mid": v(42.35, 18.53) * mm, "end": v(43.25, 16.29) * mm});
            skPoint(sketch, "E81.visualSharp", {"position": v(42.66, 11.97) * mm});
            skArc(sketch, "E81.filletArc", {"start": v(39.8, 10.26) * mm, "mid": v(40.78, 11.97) * mm, "end": v(39.8, 13.69) * mm});
            skPoint(sketch, "E82.visualSharp", {"position": v(30.54, 19.24) * mm});
            skArc(sketch, "E82.filletArc", {"start": v(33.57, 17.43) * mm, "mid": v(31.55, 17.45) * mm, "end": v(30.54, 15.71) * mm});
            skPoint(sketch, "E83.visualSharp", {"position": v(30.54, 4.7) * mm});
            skArc(sketch, "E83.filletArc", {"start": v(30.54, 8.23) * mm, "mid": v(31.55, 6.49) * mm, "end": v(33.57, 6.51) * mm});
            skPoint(sketch, "E84.visualSharp", {"position": v(46.55, 9.64) * mm});
            skArc(sketch, "E84.filletArc", {"start": v(47.58, 9.02) * mm, "mid": v(46.55, 9.3) * mm, "end": v(45.52, 9.01) * mm});
            skPoint(sketch, "E85.visualSharp", {"position": v(37.25, 4) * mm});
            skArc(sketch, "E85.filletArc", {"start": v(43.37, 7.71) * mm, "mid": v(42.48, 5.46) * mm, "end": v(44.4, 4) * mm});
            skPoint(sketch, "E86.visualSharp", {"position": v(55.95, 4) * mm});
            skArc(sketch, "E86.filletArc", {"start": v(48.73, 4) * mm, "mid": v(50.65, 5.47) * mm, "end": v(49.75, 7.71) * mm});
            skPoint(sketch, "E87.visualSharp", {"position": v(50.42, 11.98) * mm});
            skArc(sketch, "E87.filletArc", {"start": v(53.25, 13.7) * mm, "mid": v(52.29, 11.99) * mm, "end": v(53.26, 10.28) * mm});
            skPoint(sketch, "E88.visualSharp", {"position": v(62.54, 19.34) * mm});
            skArc(sketch, "E88.filletArc", {"start": v(62.54, 15.78) * mm, "mid": v(61.52, 17.53) * mm, "end": v(59.5, 17.5) * mm});
            skPoint(sketch, "E89.visualSharp", {"position": v(62.54, 4.7) * mm});
            skArc(sketch, "E89.filletArc", {"start": v(59.51, 6.53) * mm, "mid": v(61.52, 6.5) * mm, "end": v(62.54, 8.24) * mm});
            skSolve(sketch);
        }
        {
            var Q0;
            Q0=makeQuery(id+"F3.boolean.opBoolean","MERGE",EDGE,{"derivedFrom":[makeQuery(id+"F1.opExtrude","SWEPT_EDGE",EDGE,{"disambiguationData":[OSD([sQuery(id+"F0.wireOp",EDGE,"E0.top"),sQuery(id+"F0.wireOp",EDGE,"E0.right")])]}),makeQuery(id+"F3.opExtrude","SWEPT_EDGE",EDGE,{"disambiguationData":[OSD([sQuery(id+"F2.wireOp",EDGE,"E7.top"),sQuery(id+"F2.wireOp",EDGE,"E7.right")])]})]});
            var Q1;
            Q1=makeQuery(id+"F7.boolean.opBoolean","MERGE",EDGE,{"derivedFrom":[makeQuery(id+"F3.boolean.opBoolean","MERGE",EDGE,{"derivedFrom":[makeQuery(id+"F1.opExtrude","SWEPT_EDGE",EDGE,{"disambiguationData":[OSD([sQuery(id+"F0.wireOp",EDGE,"E0.top"),sQuery(id+"F0.wireOp",EDGE,"E0.left")])]}),makeQuery(id+"F3.opExtrude","SWEPT_EDGE",EDGE,{"disambiguationData":[OSD([sQuery(id+"F2.wireOp",EDGE,"E7.top"),sQuery(id+"F2.wireOp",EDGE,"E7.left")])]})]}),makeQuery(id+"F7.opExtrude","CAP_EDGE",EDGE,{"disambiguationData":[OSD([sQuery(id+"F6.wireOp",EDGE,"E20")])],"isStart":true})]});
            var Q2;
            Q2=makeQuery(id+"F1.opExtrude","CAP_EDGE",EDGE,{"disambiguationData":[OSD([sQuery(id+"F0.wireOp",EDGE,"E0.top")])],"isStart":true});
            var Q3;
            Q3=makeQuery(id+"F1.opExtrude","CAP_EDGE",EDGE,{"disambiguationData":[OSD([sQuery(id+"F0.wireOp",EDGE,"E0.right")])],"isStart":true});
            var Q4;
            Q4=makeQuery(id+"F1.opExtrude","CAP_EDGE",EDGE,{"disambiguationData":[OSD([sQuery(id+"F0.wireOp",EDGE,"E0.left")])],"isStart":true});
            var Q5;
            Q5=makeQuery(id+"F1.opExtrude","CAP_EDGE",EDGE,{"disambiguationData":[OSD([sQuery(id+"F0.wireOp",EDGE,"E0.bottom")])],"isStart":true});
            var Q6;
            Q6=makeQuery(id+"F5.boolean.opBoolean","MERGE",EDGE,{"derivedFrom":[makeQuery(id+"F3.boolean.opBoolean","MERGE",EDGE,{"derivedFrom":[makeQuery(id+"F1.opExtrude","SWEPT_EDGE",EDGE,{"disambiguationData":[OSD([sQuery(id+"F0.wireOp",EDGE,"E0.bottom"),sQuery(id+"F0.wireOp",EDGE,"E0.left")])]}),makeQuery(id+"F3.opExtrude","SWEPT_EDGE",EDGE,{"disambiguationData":[OSD([sQuery(id+"F2.wireOp",EDGE,"E7.bottom"),sQuery(id+"F2.wireOp",EDGE,"E7.left")])]})]}),makeQuery(id+"F5.opExtrude","CAP_EDGE",EDGE,{"disambiguationData":[OSD([sQuery(id+"F4.wireOp",EDGE,"E9")])],"isStart":true})]});
            var Q7;
            Q7=makeQuery(id+"F3.boolean.opBoolean","MERGE",EDGE,{"derivedFrom":[makeQuery(id+"F1.opExtrude","SWEPT_EDGE",EDGE,{"disambiguationData":[OSD([sQuery(id+"F0.wireOp",EDGE,"E0.bottom"),sQuery(id+"F0.wireOp",EDGE,"E0.right")])]}),makeQuery(id+"F3.opExtrude","SWEPT_EDGE",EDGE,{"disambiguationData":[OSD([sQuery(id+"F2.wireOp",EDGE,"E7.bottom"),sQuery(id+"F2.wireOp",EDGE,"E7.right")])]})]});
            fillet(context, id + "F20", {"entities" : qUnion([Q0, Q1, Q2, Q3, Q4, Q5, Q6, Q7]), "radius" : 2 * mm, "tangentPropagation" : true, "allowEdgeOverflow" : false});
        }
        {
            var Q0;
            Q0=makeQuery(id+"F19.imprint","IMPRINT",FACE,{"disambiguationData":[TD([[makeQuery(id+"F19.imprint","IMPRINT",EDGE,{"derivedFrom":sQuery(id+"F19.wireOp",EDGE,"E63.0")}),1.0]])]});
            var Q1;
            Q1=makeQuery(id+"F19.imprint","IMPRINT",FACE,{"disambiguationData":[TD([[makeQuery(id+"F19.imprint","IMPRINT",EDGE,{"derivedFrom":sQuery(id+"F19.wireOp",EDGE,"E69.trimOffspring")}),1.0]])]});
            var Q2;
            Q2=makeQuery(id+"F19.imprint","IMPRINT",FACE,{"disambiguationData":[TD([[makeQuery(id+"F19.imprint","IMPRINT",EDGE,{"derivedFrom":sQuery(id+"F19.wireOp",EDGE,"E66.trimOffspring")}),-1.0]])]});
            var Q3;
            Q3=makeQuery(id+"F19.imprint","IMPRINT",FACE,{"disambiguationData":[TD([[makeQuery(id+"F19.imprint","IMPRINT",EDGE,{"derivedFrom":sQuery(id+"F19.wireOp",EDGE,"E62.0")}),-1.0]])]});
            var Q4;
            {var subQ0=sQuery(id+"F2.wireOp",EDGE,"E7.bottom");Q4=makeQuery(id+"F5.boolean.opBoolean","MERGE",FACE,{"derivedFrom":[makeQuery(id+"F3.boolean.opBoolean","MERGE",FACE,{"derivedFrom":[makeQuery(id+"F1.opExtrude","SWEPT_FACE",FACE,{"disambiguationData":[OSD([sQuery(id+"F0.wireOp",EDGE,"E0.bottom")])]}),makeQuery(id+"F3.opExtrude","SWEPT_FACE",FACE,{"disambiguationData":[OSD([subQ0])]})]}),makeQuery(id+"F5.opExtrude","CAP_FACE",FACE,{"disambiguationData":[OSD([subQ0,sQuery(id+"F4.wireOp",EDGE,"E9"),sQuery(id+"F4.wireOp",EDGE,"E10"),sQuery(id+"F4.wireOp",EDGE,"E11")])],"isStart":true}),makeQuery(id+"F5.opExtrude","CAP_FACE",FACE,{"disambiguationData":[OSD([subQ0,sQuery(id+"F4.wireOp",EDGE,"E12.MirrorCS"),sQuery(id+"F4.wireOp",EDGE,"E13.MirrorCS"),sQuery(id+"F4.wireOp",EDGE,"E14.MirrorCS")])],"isStart":true})]});}
            extrude(context, id + "F21", {"entities" : qUnion([Q0, Q1, Q2, Q3]), "operationType" : NewBodyOperationType.REMOVE, "endBound" : BoundingType.UP_TO_SURFACE, "oppositeDirection" : true, "depth" : 25 * mm, "endBoundEntityFace" : qUnion([Q4]), "offsetDistance" : 25 * mm});
        }
        {
            var Q0;
            Q0=makeQuery(id+"F7.opExtrude","CAP_EDGE",EDGE,{"disambiguationData":[OSD([sQuery(id+"F6.wireOp",EDGE,"E16")])],"isStart":true});
            var Q1;
            Q1=makeQuery(id+"F7.opExtrude","CAP_EDGE",EDGE,{"disambiguationData":[OSD([sQuery(id+"F6.wireOp",EDGE,"E19")])],"isStart":true});
            var Q2;
            Q2=makeQuery(id+"F7.opExtrude","TWEAK_EDGE",EDGE,{"derivedFrom":[makeQuery(id+"F3.opExtrude","SWEPT_FACE",FACE,{"disambiguationData":[OSD([sQuery(id+"F2.wireOp",EDGE,"E8.3")])]}),makeQuery(id+"F6.imprint","IMPRINT",EDGE,{"derivedFrom":sQuery(id+"F6.wireOp",EDGE,"E19")})]});
            var Q3;
            Q3=makeQuery(id+"F5.opExtrude","CAP_EDGE",EDGE,{"disambiguationData":[OSD([sQuery(id+"F4.wireOp",EDGE,"E12.MirrorCS")])],"isStart":true});
            var Q4;
            Q4=makeQuery(id+"F5.opExtrude","CAP_EDGE",EDGE,{"disambiguationData":[OSD([sQuery(id+"F4.wireOp",EDGE,"E10")])],"isStart":true});
            var Q5;
            Q5=makeQuery(id+"F7.opExtrude","TWEAK_EDGE",EDGE,{"derivedFrom":[makeQuery(id+"F3.opExtrude","SWEPT_FACE",FACE,{"disambiguationData":[OSD([sQuery(id+"F2.wireOp",EDGE,"E8.3")])]}),makeQuery(id+"F6.imprint","IMPRINT",EDGE,{"derivedFrom":sQuery(id+"F6.wireOp",EDGE,"E16")})]});
            var Q6;
            Q6=makeQuery(id+"F5.opExtrude","TWEAK_EDGE",EDGE,{"derivedFrom":[makeQuery(id+"F3.opExtrude","SWEPT_FACE",FACE,{"disambiguationData":[OSD([sQuery(id+"F2.wireOp",EDGE,"E8.1")])]}),makeQuery(id+"F4.imprint","IMPRINT",EDGE,{"derivedFrom":sQuery(id+"F4.wireOp",EDGE,"E12.MirrorCS")})]});
            var Q7;
            Q7=makeQuery(id+"F5.opExtrude","TWEAK_EDGE",EDGE,{"derivedFrom":[makeQuery(id+"F3.opExtrude","SWEPT_FACE",FACE,{"disambiguationData":[OSD([sQuery(id+"F2.wireOp",EDGE,"E8.1")])]}),makeQuery(id+"F4.imprint","IMPRINT",EDGE,{"derivedFrom":sQuery(id+"F4.wireOp",EDGE,"E10")})]});
            fillet(context, id + "F22", {"entities" : qUnion([Q0, Q1, Q2, Q3, Q4, Q5, Q6, Q7]), "radius" : 1 * mm, "tangentPropagation" : true, "allowEdgeOverflow" : false});
        }
    });
